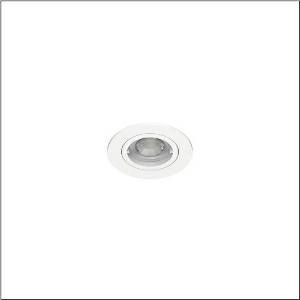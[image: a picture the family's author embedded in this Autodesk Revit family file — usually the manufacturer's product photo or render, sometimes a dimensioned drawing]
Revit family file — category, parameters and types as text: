
# Revit family: lunis_41_spot_51dt137a41a
name_source: partatom
category: Lighting Fixtures
units: mm (PartAtom-declared; Revit-internal decimal feet)

## family parameters
Cut with Voids When Loaded = No
Host = Face
Light Source = No
Part Type = Normal
Room Calculation Point = No
Round Connector Dimension = Use Diameter
Shared = No

## types (1)
- Lunis 41 Spot (1 x LED, 550 lm, 5 W, 4000K)
    Apparent Load = 5 VA
    CIE Flux Codes = 87 97 99 100 100
    Color Rendering = 80
    Color Temperature = 4000K
    Default Elevation = 1800 mm
    Description = Lunis 41,  Spot, downlight, light emission: direct distribution, LED rated luminous flux: 550lm, light colour: 840, control gear: ECG, mains connection: 230V, AC, 50/60Hz, housing, round, of aluminium, coated, traffic white (RAL 9016), diameter: 88mm, recess depth: 54mm, protection rating (complete): IP20, insulation class (complete): insulation class II (safety insulation), certification: CE, permissible ambient temperature for indoor applications: -20..+40°C, packaging unit: 1 piece
    Height = 0 mm  [stored 0 ft]
    Lamp = 1 x LED
    Lamp Light Flux = 550 lm
    Lamp Power = 5 W
    Lamp count = 1
    Length = 88 mm
    Luminous efficacy = 110 lm/W
    Manufacturer = Siteco
    ModVariant = No
    Model = 51DT137A41A
    Mounting Place = Ceiling
    Mounting Type = Recessed
    Number of Poles = 1
    OnlyDefault = Yes
    Power Factor = 1
    Product Name = Lunis 41 Spot
    Product group = downlight | ceiling recessed
    ProductGroupID = 402
    Protection Class = Protection class II
    Protection Degree = IP 20
    RLX_Detail_Level = 1
    RlxData = <blob elided: 38025 chars, md5=c641dcf8>
    Socket = socket
    Standby Power = 0 W
    System Light Flux = 550 lm
    System Power = 5 W
    Type Comments = Product without accessories
    Type Image = l_1005286.jpg
    URL = http://relux.com
    VarID = ---
    Voltage = 0 V
    Weight = 0.00 kg
    Width = 0 mm  [stored 0 ft]

note: [stored X ft] marks values corroborated as IEEE doubles in the binary element streams (Revit-internal decimal feet)

## geometry (parser evidence)
native form markers: Blend x4, Sweep x10
no freeform markers — native parametric forms only
